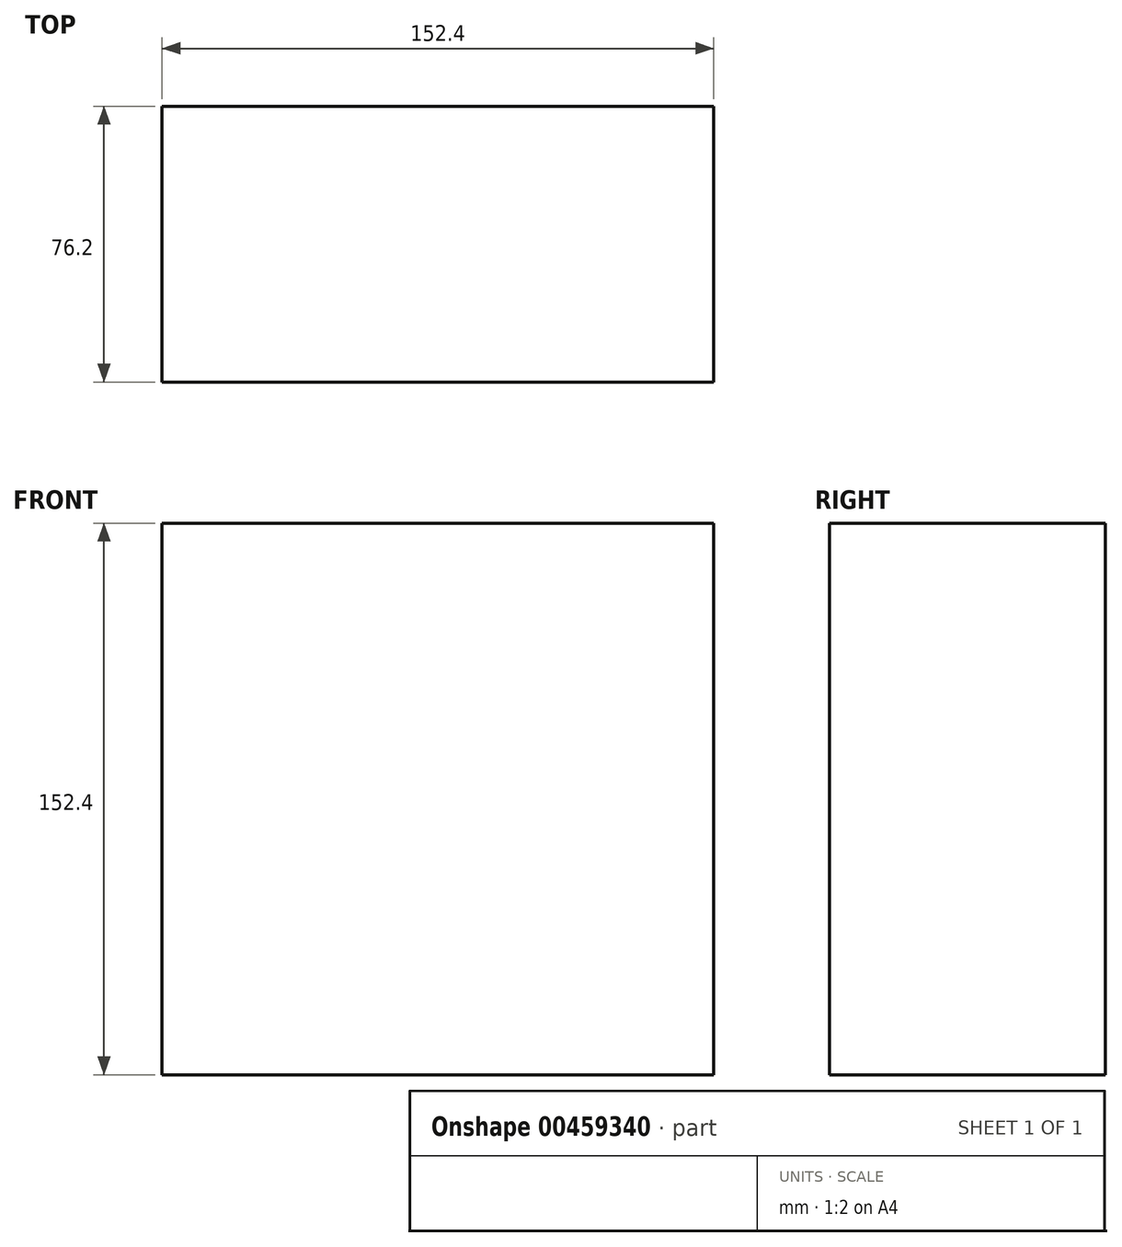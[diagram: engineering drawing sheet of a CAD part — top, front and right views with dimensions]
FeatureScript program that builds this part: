
annotation { "Feature Type Name" : "Feature", "Feature Type Description" : "" }
export const myFeature = defineFeature(function(context is Context, id is Id, definition is map)
    precondition{}
    {
        {
            var Q0;
            Q0=qCreatedBy(makeId("Top.planeOp"),FACE);
            var sketch = newSketch(context, id + "F0", { "sketchPlane" : qUnion([Q0])});
            skLineSegment(sketch, "E0.bottom", {"start": v(-114.3, 76.2) * mm, "end": v(114.3, 76.2) * mm});
            skLineSegment(sketch, "E0.top", {"start": v(-114.3, -76.2) * mm, "end": v(114.3, -76.2) * mm});
            skLineSegment(sketch, "E0.left", {"start": v(-114.3, 76.2) * mm, "end": v(-114.3, -76.2) * mm});
            skLineSegment(sketch, "E0.right", {"start": v(114.3, 76.2) * mm, "end": v(114.3, -76.2) * mm});
            skPoint(sketch, "E0.middle", {"position": v(0, 0) * mm});
            skLineSegment(sketch, "E1.bottom", {"start": v(114.3, 76.2) * mm, "end": v(-38.1, 76.2) * mm});
            skLineSegment(sketch, "E1.top", {"start": v(114.3, 0) * mm, "end": v(-38.1, 0) * mm});
            skLineSegment(sketch, "E1.left", {"start": v(114.3, 76.2) * mm, "end": v(114.3, 0) * mm});
            skLineSegment(sketch, "E1.right", {"start": v(-38.1, 76.2) * mm, "end": v(-38.1, 0) * mm});
            skSolve(sketch);
        }
        {
            var Q0;
            Q0=makeQuery(id+"F0.imprint","IMPRINT",FACE,{"disambiguationData":[TD([[makeQuery(id+"F0.imprint","IMPRINT",EDGE,{"derivedFrom":sQuery(id+"F0.wireOp",EDGE,"E0.bottom")}),-1.0]])]});
            extrude(context, id + "F1", {"entities" : qUnion([Q0]), "endBound" : BoundingType.SYMMETRIC, "depth" : 152.4 * mm});
        }
        {
            var Q0;
            Q0=makeQuery(id+"F1.opExtrude","SWEPT_FACE",FACE,{"disambiguationData":[OSD([sQuery(id+"F0.wireOp",EDGE,"E1.top")])]});
            var sketch = newSketch(context, id + "F2", { "sketchPlane" : qUnion([Q0])});
            skPoint(sketch, "E2", {"position": v(-63.5, 0) * mm});
            skSolve(sketch);
        }
        {
            var Q0;
            Q0=sQuery(id+"F2.wireOp",VERTEX,"E2");
            var Q1;
            Q1=makeQuery(id+"F1.opExtrude","SWEPT_BODY",BODY,{"disambiguationData":[OSD([sQuery(id+"F0.wireOp",EDGE,"E0.bottom"),sQuery(id+"F0.wireOp",EDGE,"E0.top"),sQuery(id+"F0.wireOp",EDGE,"E0.left"),sQuery(id+"F0.wireOp",EDGE,"E0.right"),sQuery(id+"F0.wireOp",EDGE,"E1.top"),sQuery(id+"F0.wireOp",EDGE,"E1.right")])]});
            hole(context, id + "F3", {"style" : HoleStyle.SIMPLE, "endStyle" : HoleEndStyle.THROUGH, "holeDiameter" : 50.8 * mm, "isTappedThrough" : true, "tappedDepth" : 12.7 * mm, "tapClearance" : 3, "locations" : qUnion([Q0]), "scope" : qUnion([Q1])});
        }
    });
